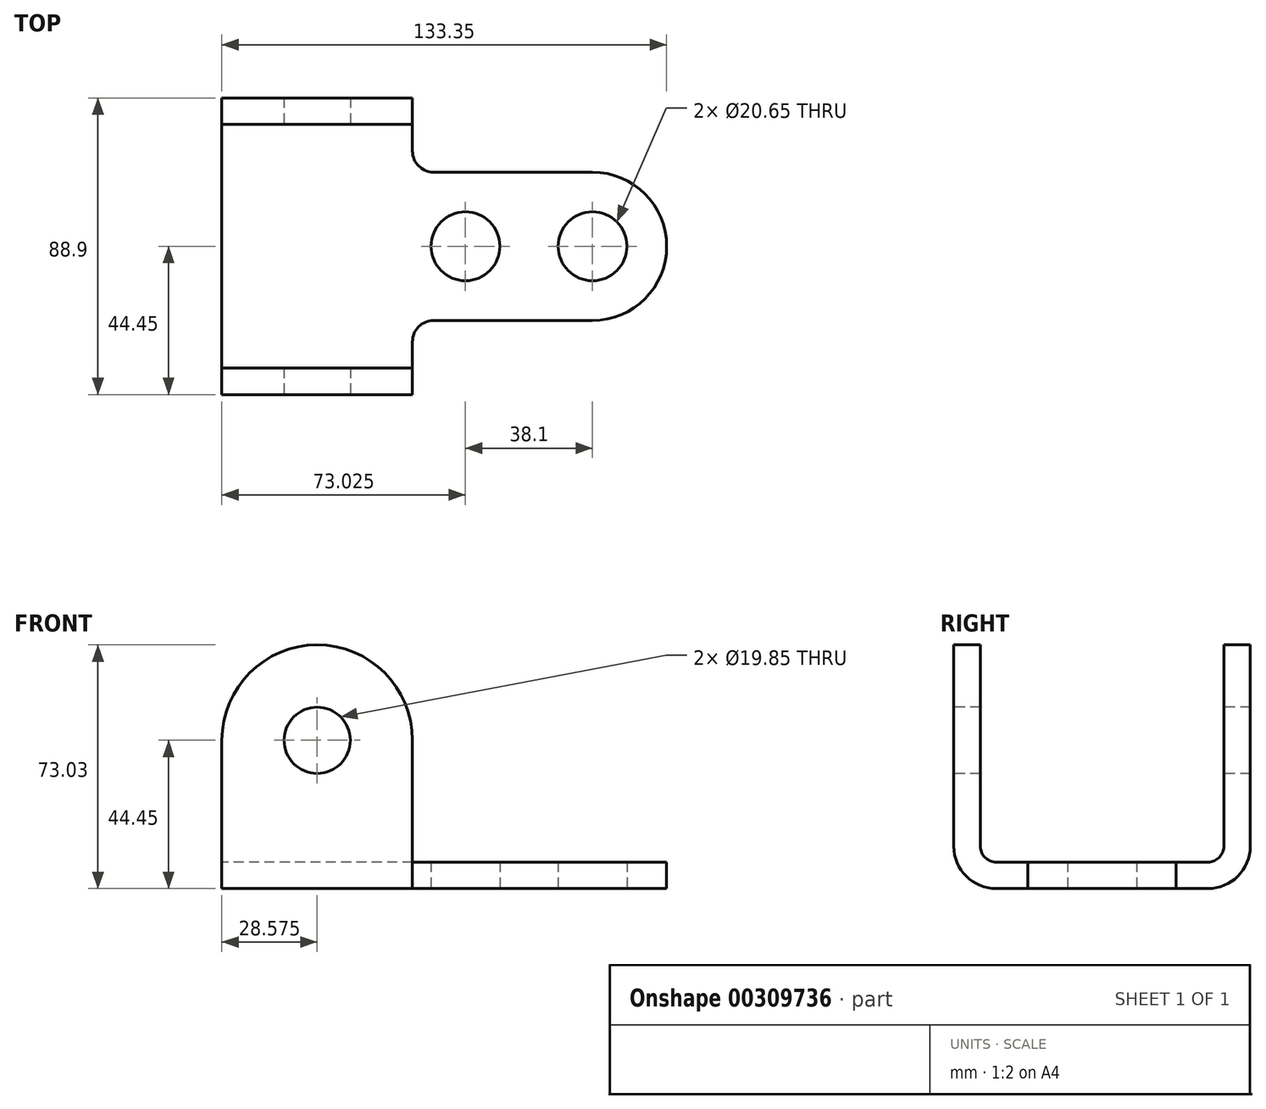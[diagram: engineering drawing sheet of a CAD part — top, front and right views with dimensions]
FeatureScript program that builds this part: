
annotation { "Feature Type Name" : "Feature", "Feature Type Description" : "" }
export const myFeature = defineFeature(function(context is Context, id is Id, definition is map)
    precondition{}
    {
        {
            var Q0;
            Q0=qCreatedBy(makeId("Top.planeOp"),FACE);
            var sketch = newSketch(context, id + "F0", { "sketchPlane" : qUnion([Q0])});
            skLineSegment(sketch, "E0", {"start": v(0, 0) * mm, "end": v(0, 88.9) * mm});
            skLineSegment(sketch, "E1", {"start": v(0, 88.9) * mm, "end": v(57.15, 88.9) * mm});
            skLineSegment(sketch, "E2", {"start": v(0, 0) * mm, "end": v(57.15, 0) * mm});
            skLineSegment(sketch, "E3", {"start": v(57.15, 0) * mm, "end": v(57.15, 15.87) * mm});
            skArc(sketch, "E4", {"start": v(57.15, 15.87) * mm, "mid": v(59, 20.37) * mm, "end": v(63.5, 22.22) * mm});
            skLineSegment(sketch, "E5", {"start": v(63.5, 66.68) * mm, "end": v(111.12, 66.68) * mm});
            skLineSegment(sketch, "E6", {"start": v(63.5, 22.23) * mm, "end": v(111.12, 22.23) * mm});
            skArc(sketch, "E7", {"start": v(111.12, 22.23) * mm, "mid": v(133.35, 44.45) * mm, "end": v(111.12, 66.68) * mm});
            skCircle(sketch, "E8", {"center": v(73.03, 44.45) * mm, "radius": 10.33 * mm});
            skCircle(sketch, "E9", {"center": v(111.12, 44.45) * mm, "radius": 10.33 * mm});
            skCircle(sketch, "E10", {"center": v(212.29, -21.03) * mm, "radius": 9.92 * mm, "construction": true});
            skLineSegment(sketch, "E11", {"start": v(183.71, -21.03) * mm, "end": v(183.71, -65.48) * mm, "construction": true});
            skLineSegment(sketch, "E12", {"start": v(183.71, -65.48) * mm, "end": v(240.86, -65.48) * mm, "construction": true});
            skLineSegment(sketch, "E13", {"start": v(240.86, -65.48) * mm, "end": v(240.86, -21.03) * mm, "construction": true});
            skLineSegment(sketch, "E14", {"start": v(212.29, -21.03) * mm, "end": v(212.29, -40.1) * mm, "construction": true});
            skArc(sketch, "E15", {"start": v(183.71, -21.03) * mm, "mid": v(212.29, 7.55) * mm, "end": v(240.86, -21.03) * mm, "construction": true});
            skLineSegment(sketch, "E16", {"start": v(57.15, 88.9) * mm, "end": v(57.15, 73.03) * mm});
            skArc(sketch, "E17", {"start": v(57.15, 73.03) * mm, "mid": v(59, 68.53) * mm, "end": v(63.5, 66.68) * mm});
            skSolve(sketch);
        }
        {
            var Q0;
            Q0 = qSketchRegion(id + "F0", true);
            extrude(context, id + "F1", {"entities" : qUnion([Q0]), "depth" : 76.2 * mm});
        }
        {
            var Q0;
            Q0=makeQuery(id+"F1.opExtrude","CAP_FACE",FACE,{"disambiguationData":[OSD([sQuery(id+"F0.wireOp",EDGE,"E0"),sQuery(id+"F0.wireOp",EDGE,"E1"),sQuery(id+"F0.wireOp",EDGE,"E2"),sQuery(id+"F0.wireOp",EDGE,"E3"),sQuery(id+"F0.wireOp",EDGE,"oBsBRglE-m7rA-JXYk-MLbt-kAHypdkcGy1t"),sQuery(id+"F0.wireOp",EDGE,"d26de93f-0ff5-4548-bb7b-9a47d6897ae4"),sQuery(id+"F0.wireOp",EDGE,"E4"),sQuery(id+"F0.wireOp",EDGE,"E5"),sQuery(id+"F0.wireOp",EDGE,"E6"),sQuery(id+"F0.wireOp",EDGE,"E7"),sQuery(id+"F0.wireOp",EDGE,"E8"),sQuery(id+"F0.wireOp",EDGE,"E9")])],"isStart":false});
            var sketch = newSketch(context, id + "F2", { "sketchPlane" : qUnion([Q0])});
            skLineSegment(sketch, "E18.0.0", {"start": v(63.5, 22.23) * mm, "end": v(111.12, 22.23) * mm});
            skArc(sketch, "E18.0.1", {"start": v(111.12, 22.23) * mm, "mid": v(133.35, 44.45) * mm, "end": v(111.12, 66.68) * mm});
            skLineSegment(sketch, "E18.0.2", {"start": v(111.12, 66.68) * mm, "end": v(63.5, 66.68) * mm});
            skLineSegment(sketch, "E18.0.6", {"start": v(0, 80.96) * mm, "end": v(0, 7.95) * mm});
            skLineSegment(sketch, "E18.0.8", {"start": v(57.15, 7.95) * mm, "end": v(57.15, 15.87) * mm});
            skArc(sketch, "E18.0.9", {"start": v(57.15, 15.87) * mm, "mid": v(59, 20.37) * mm, "end": v(63.5, 22.22) * mm});
            skLineSegment(sketch, "E19", {"start": v(57.15, 7.95) * mm, "end": v(0, 7.95) * mm});
            skLineSegment(sketch, "E20", {"start": v(0, 44.45) * mm, "end": v(28.8, 44.45) * mm, "construction": true});
            skLineSegment(sketch, "E21.MirrorCS", {"start": v(57.15, 80.96) * mm, "end": v(0, 80.96) * mm});
            skPoint(sketch, "E22.orphan", {"position": v(0, 88.9) * mm});
            skPoint(sketch, "E18.0.7.end.orphan", {"position": v(57.15, 0) * mm});
            skPoint(sketch, "E18.0.7.start.orphan", {"position": v(0, 0) * mm});
            skArc(sketch, "E23.0.1", {"start": v(63.5, 66.68) * mm, "mid": v(59, 68.53) * mm, "end": v(57.15, 73.03) * mm});
            skLineSegment(sketch, "E23.0.2", {"start": v(57.15, 73.03) * mm, "end": v(57.15, 80.96) * mm});
            skPoint(sketch, "E24.orphan", {"position": v(57.15, 88.9) * mm});
            skSolve(sketch);
        }
        {
            var Q0;
            Q0 = qSketchRegion(id + "F2", true);
            extrude(context, id + "F3", {"entities" : qUnion([Q0]), "operationType" : NewBodyOperationType.REMOVE, "oppositeDirection" : true, "depth" : 68.26 * mm});
        }
        {
            var Q0;
            Q0=makeQuery(id+"F1.opExtrude","SWEPT_FACE",FACE,{"disambiguationData":[OSD([sQuery(id+"F0.wireOp",EDGE,"E2")])]});
            var sketch = newSketch(context, id + "F4", { "sketchPlane" : qUnion([Q0])});
            skCircle(sketch, "E25", {"center": v(28.58, 44.45) * mm, "radius": 9.92 * mm});
            skLineSegment(sketch, "E26", {"start": v(28.58, 44.45) * mm, "end": v(28.58, 25.26) * mm, "construction": true});
            skArc(sketch, "E27", {"start": v(0, 44.45) * mm, "mid": v(28.58, 73.03) * mm, "end": v(57.15, 44.45) * mm});
            skLineSegment(sketch, "E28", {"start": v(0, 44.45) * mm, "end": v(0, 76.2) * mm});
            skLineSegment(sketch, "E29", {"start": v(0, 76.2) * mm, "end": v(57.15, 76.2) * mm});
            skLineSegment(sketch, "E30", {"start": v(57.15, 76.2) * mm, "end": v(57.15, 44.45) * mm});
            skSolve(sketch);
        }
        {
            var Q0;
            Q0 = qSketchRegion(id + "F4", true);
            extrude(context, id + "F5", {"entities" : qUnion([Q0]), "operationType" : NewBodyOperationType.REMOVE, "endBound" : BoundingType.THROUGH_ALL, "oppositeDirection" : true, "depth" : 25.4 * mm});
        }
        {
            var Q0;
            Q0=makeQuery(id+"F1.opExtrude","CAP_EDGE",EDGE,{"disambiguationData":[OSD([sQuery(id+"F0.wireOp",EDGE,"E2")])],"isStart":true});
            var Q1;
            Q1=makeQuery(id+"F1.opExtrude","CAP_EDGE",EDGE,{"disambiguationData":[OSD([sQuery(id+"F0.wireOp",EDGE,"E1")])],"isStart":true});
            fillet(context, id + "F6", {"entities" : qUnion([Q0, Q1]), "radius" : 12.7 * mm, "tangentPropagation" : true, "allowEdgeOverflow" : false});
        }
        {
            var Q0;
            Q0=makeQuery(id+"F3.boolean.opBoolean","COPY",EDGE,{"derivedFrom":makeQuery(id+"F3.opExtrude","CAP_EDGE",EDGE,{"disambiguationData":[OSD([sQuery(id+"F2.wireOp",EDGE,"E19")])],"isStart":false})});
            var Q1;
            Q1=makeQuery(id+"F3.boolean.opBoolean","COPY",EDGE,{"derivedFrom":makeQuery(id+"F3.opExtrude","CAP_EDGE",EDGE,{"disambiguationData":[OSD([sQuery(id+"F2.wireOp",EDGE,"E21.MirrorCS")])],"isStart":false})});
            fillet(context, id + "F7", {"entities" : qUnion([Q0, Q1]), "radius" : 4.76 * mm, "tangentPropagation" : true, "allowEdgeOverflow" : false});
        }
    });
